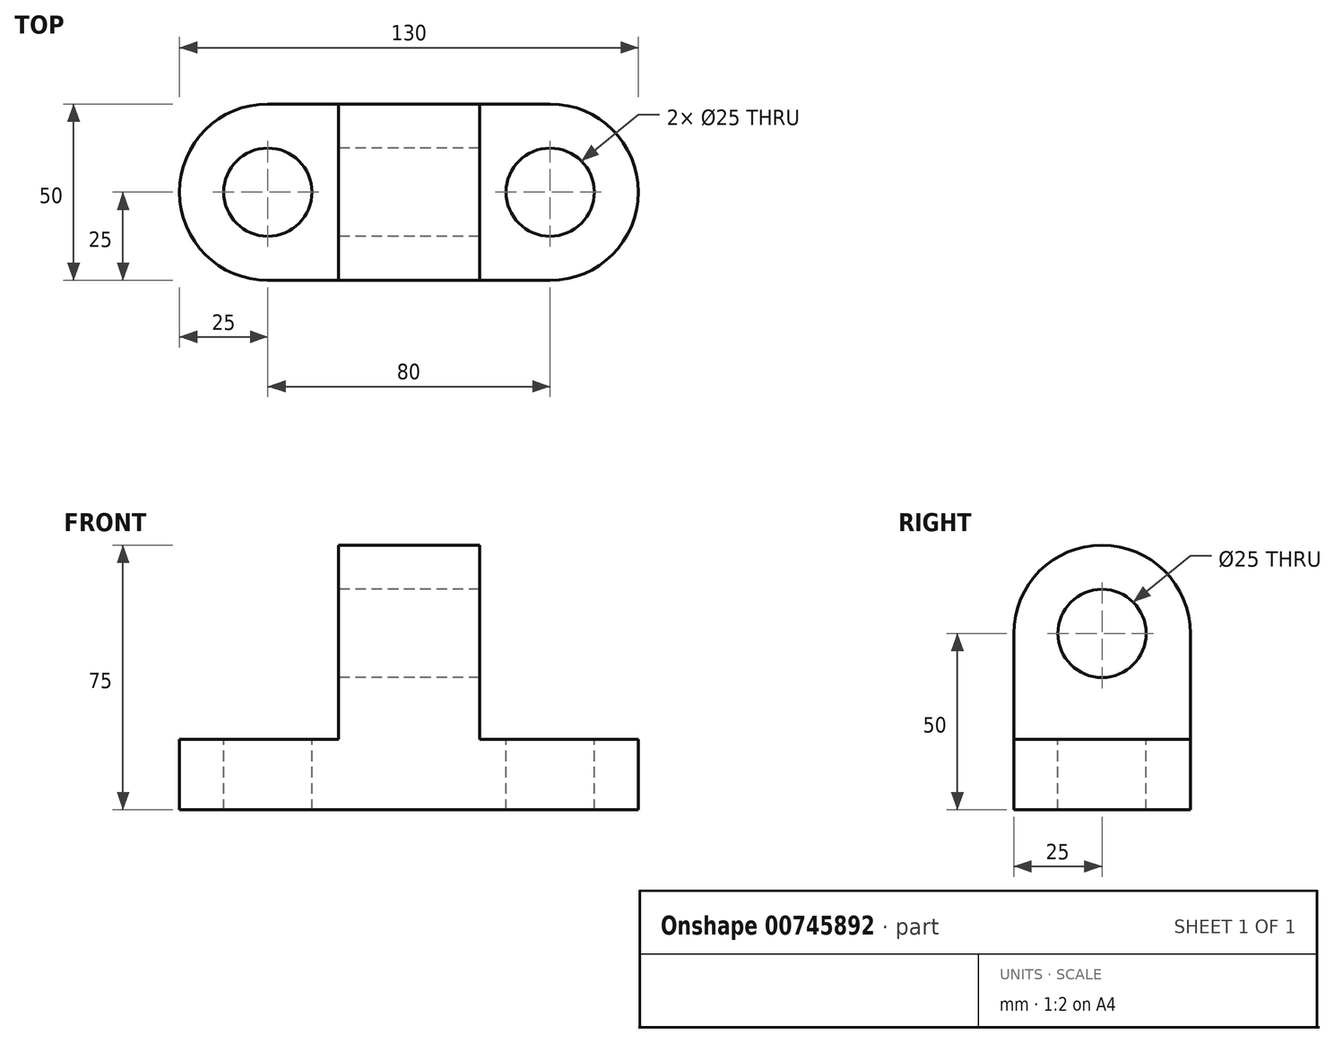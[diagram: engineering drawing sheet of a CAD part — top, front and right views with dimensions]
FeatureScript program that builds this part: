
annotation { "Feature Type Name" : "Feature", "Feature Type Description" : "" }
export const myFeature = defineFeature(function(context is Context, id is Id, definition is map)
    precondition{}
    {
        {
            var Q0;
            Q0=qCreatedBy(makeId("Front.planeOp"),FACE);
            var sketch = newSketch(context, id + "F0", { "sketchPlane" : qUnion([Q0])});
            skLineSegment(sketch, "E0", {"start": v(0, 0) * mm, "end": v(40, 0) * mm});
            skLineSegment(sketch, "E1", {"start": v(40, 0) * mm, "end": v(40, 50) * mm});
            skLineSegment(sketch, "E2", {"start": v(40, 50) * mm, "end": v(0, 50) * mm});
            skLineSegment(sketch, "E3", {"start": v(0, 50) * mm, "end": v(0, 0) * mm});
            skLineSegment(sketch, "E4", {"start": v(0, 0) * mm, "end": v(-20, 0) * mm});
            skLineSegment(sketch, "E5", {"start": v(-20, 0) * mm, "end": v(-20, 20) * mm});
            skLineSegment(sketch, "E6", {"start": v(-20, 20) * mm, "end": v(0, 20) * mm});
            skLineSegment(sketch, "E7", {"start": v(40, 0) * mm, "end": v(60, 0) * mm});
            skLineSegment(sketch, "E8", {"start": v(60, 0) * mm, "end": v(60, 20) * mm});
            skLineSegment(sketch, "E9", {"start": v(60, 20) * mm, "end": v(40, 20) * mm});
            skSolve(sketch);
        }
        {
            var Q0;
            Q0 = qSketchRegion(id + "F0", true);
            extrude(context, id + "F1", {"entities" : qUnion([Q0]), "depth" : 25 * mm, "offsetDistance" : 25 * mm});
        }
        {
            var Q0;
            Q0=makeQuery(id+"F1.opExtrude","CAP_FACE",FACE,{"disambiguationData":[OSD([sQuery(id+"F0.wireOp",EDGE,"E0"),sQuery(id+"F0.wireOp",EDGE,"E1"),sQuery(id+"F0.wireOp",EDGE,"E2"),sQuery(id+"F0.wireOp",EDGE,"E3"),sQuery(id+"F0.wireOp",EDGE,"E4"),sQuery(id+"F0.wireOp",EDGE,"E5"),sQuery(id+"F0.wireOp",EDGE,"E6"),sQuery(id+"F0.wireOp",EDGE,"E7"),sQuery(id+"F0.wireOp",EDGE,"E8"),sQuery(id+"F0.wireOp",EDGE,"E9")])],"isStart":false});
            extrude(context, id + "F2", {"entities" : qUnion([Q0]), "operationType" : NewBodyOperationType.ADD, "depth" : 25 * mm, "offsetDistance" : 25 * mm});
        }
        {
            var Q0;
            {var subQ0=sQuery(id+"F0.wireOp",EDGE,"E7");var subQ1=sQuery(id+"F0.wireOp",EDGE,"E4");var subQ2=sQuery(id+"F0.wireOp",EDGE,"E0");Q0=makeQuery(id+"F2.boolean.opBoolean","MERGE",FACE,{"derivedFrom":[makeQuery(id+"F1.opExtrude","SWEPT_FACE",FACE,{"disambiguationData":[OSD([subQ2,subQ1,subQ0])]}),makeQuery(id+"F2.opExtrude","SWEPT_FACE",FACE,{"disambiguationData":[OSD([subQ2,subQ1,subQ0])]})]});}
            var sketch = newSketch(context, id + "F3", { "sketchPlane" : qUnion([Q0])});
            skArc(sketch, "E10", {"start": v(60, 0) * mm, "mid": v(85, 25) * mm, "end": v(60, 50) * mm});
            skArc(sketch, "E11", {"start": v(-20, 50) * mm, "mid": v(-45, 25) * mm, "end": v(-20, 0) * mm});
            skSolve(sketch);
        }
        {
            var Q0;
            Q0=makeQuery(id+"F3.imprint","IMPRINT",FACE,{"disambiguationData":[TD([[makeQuery(id+"F3.imprint","IMPRINT",EDGE,{"derivedFrom":sQuery(id+"F3.wireOp",EDGE,"E11")}),1.0]])]});
            var Q1;
            Q1=makeQuery(id+"F3.imprint","IMPRINT",FACE,{"disambiguationData":[TD([[makeQuery(id+"F3.imprint","IMPRINT",EDGE,{"derivedFrom":sQuery(id+"F3.wireOp",EDGE,"E10")}),1.0]])]});
            extrude(context, id + "F4", {"entities" : qUnion([Q0, Q1]), "operationType" : NewBodyOperationType.ADD, "oppositeDirection" : true, "depth" : 20 * mm, "offsetDistance" : 25 * mm});
        }
        {
            var Q0;
            {var subQ0=sQuery(id+"F0.wireOp",EDGE,"E1");Q0=makeQuery(id+"F2.boolean.opBoolean","MERGE",FACE,{"derivedFrom":[makeQuery(id+"F1.opExtrude","SWEPT_FACE",FACE,{"disambiguationData":[OSD([subQ0])]}),makeQuery(id+"F2.opExtrude","SWEPT_FACE",FACE,{"disambiguationData":[OSD([subQ0])]})]});}
            var sketch = newSketch(context, id + "F5", { "sketchPlane" : qUnion([Q0])});
            skArc(sketch, "E12", {"start": v(0, 50) * mm, "mid": v(-25, 75) * mm, "end": v(-50, 50) * mm});
            skSolve(sketch);
        }
        {
            var Q0;
            Q0=makeQuery(id+"F5.imprint","IMPRINT",FACE,{"disambiguationData":[TD([[makeQuery(id+"F5.imprint","IMPRINT",EDGE,{"derivedFrom":sQuery(id+"F5.wireOp",EDGE,"E12")}),1.0]])]});
            extrude(context, id + "F6", {"entities" : qUnion([Q0]), "operationType" : NewBodyOperationType.ADD, "oppositeDirection" : true, "depth" : 40 * mm, "offsetDistance" : 25 * mm});
        }
        {
            var Q0;
            {var subQ0=sQuery(id+"F0.wireOp",EDGE,"E9");Q0=makeQuery(id+"F4.boolean.opBoolean","MERGE",FACE,{"derivedFrom":[makeQuery(id+"F2.boolean.opBoolean","MERGE",FACE,{"derivedFrom":[makeQuery(id+"F1.opExtrude","SWEPT_FACE",FACE,{"disambiguationData":[OSD([subQ0])]}),makeQuery(id+"F2.opExtrude","SWEPT_FACE",FACE,{"disambiguationData":[OSD([subQ0])]})]}),makeQuery(id+"F4.opExtrude","CAP_FACE",FACE,{"disambiguationData":[OSD([sQuery(id+"F0.wireOp",EDGE,"E7"),sQuery(id+"F0.wireOp",EDGE,"E8"),sQuery(id+"F3.wireOp",EDGE,"E10")])],"isStart":false})]});}
            var sketch = newSketch(context, id + "F7", { "sketchPlane" : qUnion([Q0])});
            skCircle(sketch, "E13", {"center": v(60, -25) * mm, "radius": 12.5 * mm});
            skSolve(sketch);
        }
        {
            var Q0;
            Q0=makeQuery(id+"F7.imprint","IMPRINT",FACE,{"disambiguationData":[TD([[makeQuery(id+"F7.imprint","IMPRINT",EDGE,{"derivedFrom":sQuery(id+"F7.wireOp",EDGE,"E13")}),1.0]])]});
            var Q1;
            Q1=sQuery(id+"F7.wireOp",EDGE,"E13");
            extrude(context, id + "F8", {"entities" : qUnion([Q0]), "operationType" : NewBodyOperationType.REMOVE, "surfaceEntities" : qUnion([Q1]), "oppositeDirection" : true, "depth" : 25 * mm, "offsetDistance" : 25 * mm});
        }
        {
            var Q0;
            {var subQ0=sQuery(id+"F0.wireOp",EDGE,"E6");Q0=makeQuery(id+"F4.boolean.opBoolean","MERGE",FACE,{"derivedFrom":[makeQuery(id+"F2.boolean.opBoolean","MERGE",FACE,{"derivedFrom":[makeQuery(id+"F1.opExtrude","SWEPT_FACE",FACE,{"disambiguationData":[OSD([subQ0])]}),makeQuery(id+"F2.opExtrude","SWEPT_FACE",FACE,{"disambiguationData":[OSD([subQ0])]})]}),makeQuery(id+"F4.opExtrude","CAP_FACE",FACE,{"disambiguationData":[OSD([sQuery(id+"F0.wireOp",EDGE,"E4"),sQuery(id+"F0.wireOp",EDGE,"E5"),sQuery(id+"F3.wireOp",EDGE,"E11")])],"isStart":false})]});}
            var sketch = newSketch(context, id + "F9", { "sketchPlane" : qUnion([Q0])});
            skCircle(sketch, "E14", {"center": v(-20, -25) * mm, "radius": 12.5 * mm});
            skSolve(sketch);
        }
        {
            var Q0;
            Q0=makeQuery(id+"F9.imprint","IMPRINT",FACE,{"disambiguationData":[TD([[makeQuery(id+"F9.imprint","IMPRINT",EDGE,{"derivedFrom":sQuery(id+"F9.wireOp",EDGE,"E14")}),1.0]])]});
            extrude(context, id + "F10", {"entities" : qUnion([Q0]), "operationType" : NewBodyOperationType.REMOVE, "oppositeDirection" : true, "depth" : 25 * mm, "offsetDistance" : 25 * mm});
        }
        {
            var Q0;
            {var subQ0=sQuery(id+"F0.wireOp",EDGE,"E3");Q0=makeQuery(id+"F6.boolean.opBoolean","MERGE",FACE,{"derivedFrom":[makeQuery(id+"F2.boolean.opBoolean","MERGE",FACE,{"derivedFrom":[makeQuery(id+"F1.opExtrude","SWEPT_FACE",FACE,{"disambiguationData":[OSD([subQ0])]}),makeQuery(id+"F2.opExtrude","SWEPT_FACE",FACE,{"disambiguationData":[OSD([subQ0])]})]}),makeQuery(id+"F6.opExtrude","CAP_FACE",FACE,{"disambiguationData":[OSD([sQuery(id+"F0.wireOp",EDGE,"E1"),sQuery(id+"F0.wireOp",EDGE,"E2"),sQuery(id+"F5.wireOp",EDGE,"E12")])],"isStart":false})]});}
            var sketch = newSketch(context, id + "F11", { "sketchPlane" : qUnion([Q0])});
            skCircle(sketch, "E15", {"center": v(25, 50) * mm, "radius": 12.5 * mm});
            skSolve(sketch);
        }
        {
            var Q0;
            Q0=makeQuery(id+"F11.imprint","IMPRINT",FACE,{"disambiguationData":[TD([[makeQuery(id+"F11.imprint","IMPRINT",EDGE,{"derivedFrom":sQuery(id+"F11.wireOp",EDGE,"E15")}),1.0]])]});
            extrude(context, id + "F12", {"entities" : qUnion([Q0]), "operationType" : NewBodyOperationType.REMOVE, "endBound" : BoundingType.THROUGH_ALL, "oppositeDirection" : true, "depth" : 25 * mm, "offsetDistance" : 25 * mm});
        }
    });
